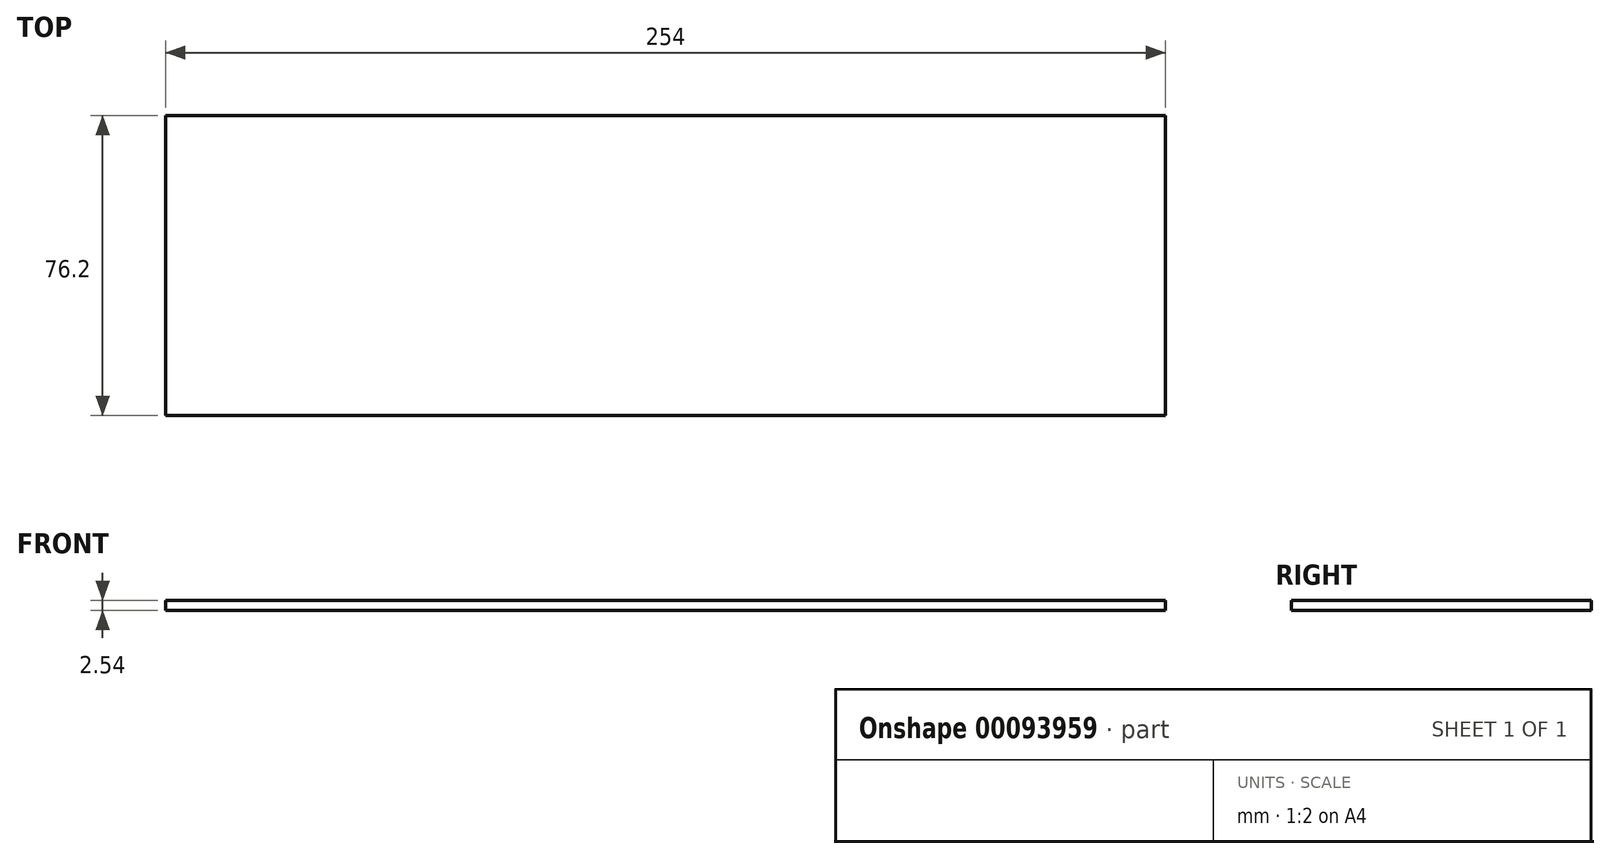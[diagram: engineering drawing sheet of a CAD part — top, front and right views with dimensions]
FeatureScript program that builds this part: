
annotation { "Feature Type Name" : "Feature", "Feature Type Description" : "" }
export const myFeature = defineFeature(function(context is Context, id is Id, definition is map)
    precondition{}
    {
        {
            var Q0;
            Q0=qCreatedBy(makeId("Top.planeOp"),FACE);
            var sketch = newSketch(context, id + "F0", { "sketchPlane" : qUnion([Q0])});
            skLineSegment(sketch, "E0.bottom", {"start": v(127, 38.1) * mm, "end": v(-127, 38.1) * mm});
            skLineSegment(sketch, "E0.top", {"start": v(127, -38.1) * mm, "end": v(-127, -38.1) * mm});
            skLineSegment(sketch, "E0.left", {"start": v(127, 38.1) * mm, "end": v(127, -38.1) * mm});
            skLineSegment(sketch, "E0.right", {"start": v(-127, 38.1) * mm, "end": v(-127, -38.1) * mm});
            skPoint(sketch, "E0.middle", {"position": v(0, 0) * mm});
            skSolve(sketch);
        }
        {
            var Q0;
            Q0=makeQuery(id+"F0.imprint","IMPRINT",FACE,{"disambiguationData":[TD([[makeQuery(id+"F0.imprint","IMPRINT",EDGE,{"derivedFrom":sQuery(id+"F0.wireOp",EDGE,"E0.bottom")}),1.0]])]});
            extrude(context, id + "F1", {"entities" : qUnion([Q0]), "depth" : 2.54 * mm});
        }
    });
